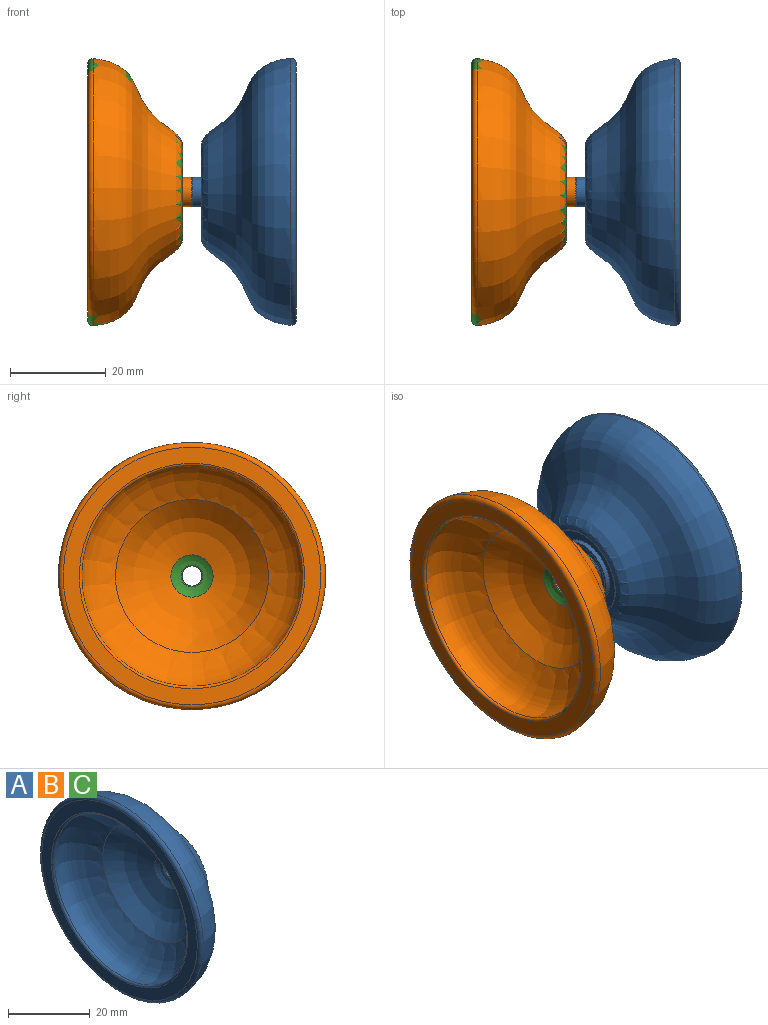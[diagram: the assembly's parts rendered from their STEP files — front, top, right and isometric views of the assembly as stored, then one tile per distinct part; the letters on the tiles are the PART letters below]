
ASSEMBLY  parts=3 mates=1
PART A: 25 faces, bbox 22x60.5x60.5 mm
  f0: plane 53.94x53.94mm, normal (-1,0,0), area 535.6mm2, adj f1,f24
  f1: torus R=23.6mm, axis (1,0,0), area 126.4mm2, adj f0,f2
  f2: revolved ~46.95x46.95mm, area 1752.1mm2, adj f1,f3
  f3: revolved ~32.04x32.04mm, area 898.8mm2, adj f2,f4
  f4: revolved ~8.84x8.84mm, area 49.7mm2, adj f3,f5
  f5: torus R=2.3mm, axis (1,0,0), area 4mm2, adj f4,f6
  f6: cylinder r=2.1mm len=4.2mm, axis (1,0,0), area 54.2mm2, adj f5,f7
  f7: torus R=2.3mm, axis (1,0,0), area 4.3mm2, adj f6,f8
  f8: plane 5.8x5.8mm, normal (1,0,0), area 9.8mm2, adj f7,f9
  f9: torus R=2.9mm, axis (1,0,0), area 6mm2, adj f8,f10
  f10: cylinder r=3.1mm len=6.2mm, axis (1,0,0), area 40.9mm2, adj f9,f11
  f11: plane 7.8x7.8mm, normal (1,0,0), area 17.6mm2, adj f10,f12
  f12: torus R=3.9mm, axis (1,0,0), area 7.9mm2, adj f11,f13
  f13: cylinder r=4.1mm len=8.2mm, axis (1,0,0), area 15.5mm2, adj f12,f14
  f14: torus R=4.3mm, axis (1,0,0), area 8.2mm2, adj f13,f15
  f15: plane 12.51x12.51mm, normal (1,0,0), area 64.8mm2, adj f14,f16
  f16: torus R=6.25mm, axis (1,0,0), area 12.4mm2, adj f15,f17
  f17: cone r=6.45mm half-angle=1.6deg, axis (1,0,0), area 38.8mm2, adj f16,f18
  f18: plane 14x14mm, normal (1,0,0), area 22mm2, adj f17,f19
  f19: cylinder r=7mm len=14mm, axis (1,0,0), area 44mm2, adj f18,f20
  f20: plane 19x19mm, normal (1,0,0), area 129.6mm2, adj f19,f21
  f21: cone r=9.5mm half-angle=0deg, axis (1,0,0), area 47.4mm2, adj f20,f22
  f22: torus R=9.7mm, axis (1,0,0), area 19.6mm2, adj f21,f23
  f23: revolved ~55.94x55.94mm, area 3457mm2, adj f22,f24
  f24: torus R=26.97mm, axis (1,0,0), area 283.2mm2, adj f0,f23
PART B: same geometry as A
PART C: same geometry as A
PLACE A rot(axis=(0,1,0),180deg) t=(137.35,3.1,-24.94)mm
PLACE B t=(-69.17,3.1,-6.11)mm
PLACE C t=(-69.17,3.1,-6.11)mm
MATE planar A.f7 <-> B.f7  axis (-1,0,0) through (34.09,3.1,-15.52)mm
